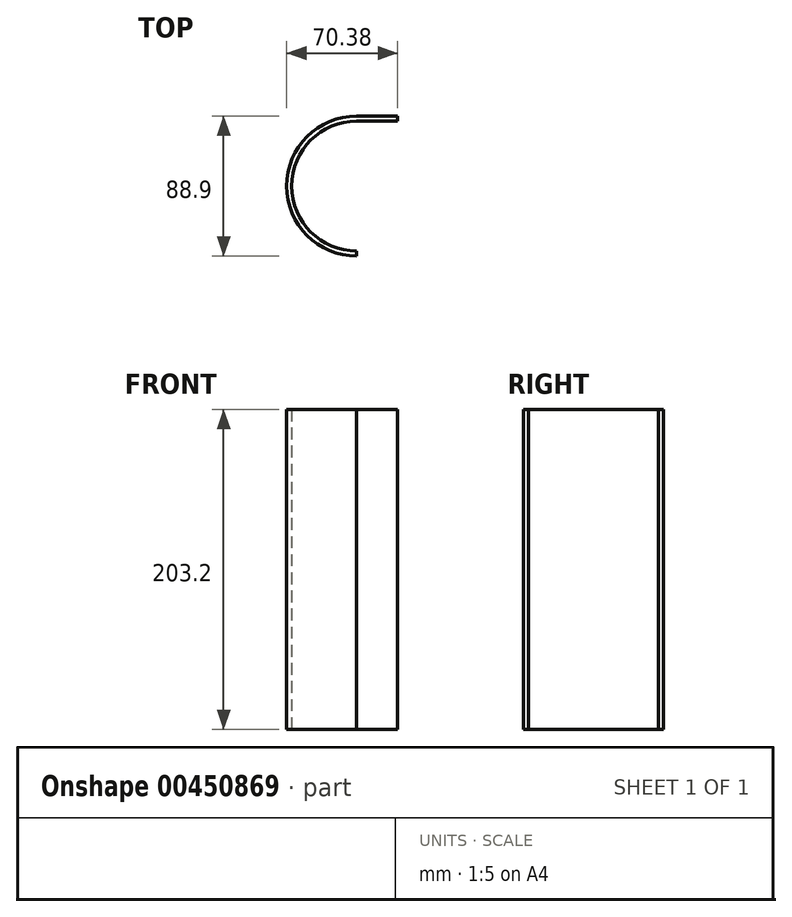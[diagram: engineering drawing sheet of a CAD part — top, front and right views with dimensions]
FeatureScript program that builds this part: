
annotation { "Feature Type Name" : "Feature", "Feature Type Description" : "" }
export const myFeature = defineFeature(function(context is Context, id is Id, definition is map)
    precondition{}
    {
        {
            var Q0;
            Q0=qCreatedBy(makeId("Top.planeOp"),FACE);
            var sketch = newSketch(context, id + "F0", { "sketchPlane" : qUnion([Q0])});
            skArc(sketch, "E0", {"start": v(0, 41.28) * mm, "mid": v(-41.28, 0) * mm, "end": v(0, -41.28) * mm});
            skLineSegment(sketch, "E1", {"start": v(0, 41.28) * mm, "end": v(0, -41.28) * mm, "construction": true});
            skPoint(sketch, "E2.orphan", {"position": v(0, 128) * mm});
            skArc(sketch, "E3.0", {"start": v(0, 44.45) * mm, "mid": v(-44.45, 0) * mm, "end": v(0, -44.45) * mm});
            skLineSegment(sketch, "E4", {"start": v(0, -41.28) * mm, "end": v(0, -44.45) * mm});
            skLineSegment(sketch, "E5", {"start": v(0, 44.45) * mm, "end": v(25.93, 44.45) * mm});
            skLineSegment(sketch, "E6", {"start": v(25.93, 44.45) * mm, "end": v(25.93, 41.28) * mm});
            skLineSegment(sketch, "E7", {"start": v(25.93, 41.28) * mm, "end": v(0, 41.28) * mm});
            skSolve(sketch);
        }
        {
            var Q0;
            Q0=qSketchRegion(id+"F0",true);
            extrude(context, id + "F1", {"entities" : qUnion([Q0]), "endBound" : BoundingType.SYMMETRIC, "depth" : 203.2 * mm});
        }
    });
